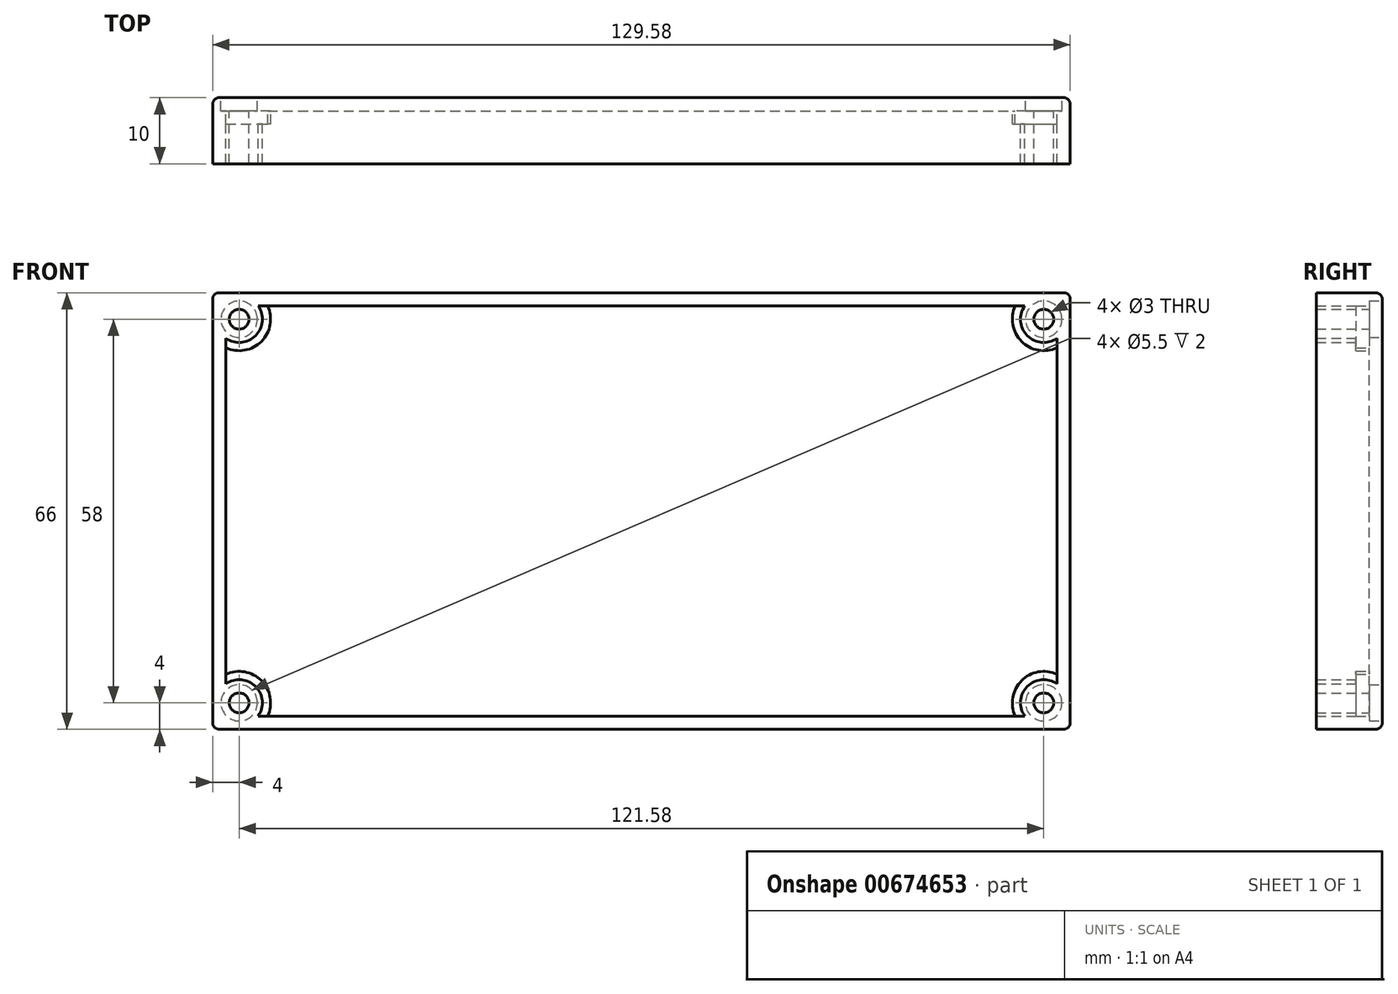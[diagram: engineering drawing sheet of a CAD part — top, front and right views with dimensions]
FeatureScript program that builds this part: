
annotation { "Feature Type Name" : "Feature", "Feature Type Description" : "" }
export const myFeature = defineFeature(function(context is Context, id is Id, definition is map)
    precondition{}
    {
        {
            var Q0;
            Q0=qCreatedBy(makeId("Front.planeOp"),FACE);
            var sketch = newSketch(context, id + "F0", { "sketchPlane" : qUnion([Q0])});
            skLineSegment(sketch, "E0.bottom", {"start": v(0, 0) * mm, "end": v(129.58, 0) * mm});
            skLineSegment(sketch, "E0.top", {"start": v(0, 66) * mm, "end": v(129.58, 66) * mm});
            skLineSegment(sketch, "E0.left", {"start": v(0, 0) * mm, "end": v(0, 66) * mm});
            skLineSegment(sketch, "E0.right", {"start": v(129.58, 0) * mm, "end": v(129.58, 66) * mm});
            skSolve(sketch);
        }
        {
            var Q0;
            Q0=makeQuery(id+"F0.imprint","IMPRINT",FACE,{"disambiguationData":[TD([[makeQuery(id+"F0.imprint","IMPRINT",EDGE,{"derivedFrom":sQuery(id+"F0.wireOp",EDGE,"E0.bottom")}),1.0]])]});
            extrude(context, id + "F1", {"entities" : qUnion([Q0]), "depth" : 10 * mm, "offsetDistance" : 25.4 * mm});
        }
        {
            var Q0;
            Q0=qCreatedBy(makeId("Front.planeOp"),FACE);
            var sketch = newSketch(context, id + "F2", { "sketchPlane" : qUnion([Q0])});
            skCircle(sketch, "E1", {"center": v(4, 62) * mm, "radius": 2.75 * mm});
            skCircle(sketch, "E2", {"center": v(125.58, 62) * mm, "radius": 2.75 * mm});
            skCircle(sketch, "E3", {"center": v(4, 4) * mm, "radius": 2.75 * mm});
            skCircle(sketch, "E4", {"center": v(125.58, 4) * mm, "radius": 2.75 * mm});
            skCircle(sketch, "E5", {"center": v(4, 62) * mm, "radius": 1.5 * mm});
            skCircle(sketch, "E6", {"center": v(4, 4) * mm, "radius": 1.5 * mm});
            skCircle(sketch, "E7", {"center": v(125.58, 4) * mm, "radius": 1.5 * mm});
            skCircle(sketch, "E8", {"center": v(125.58, 62) * mm, "radius": 1.5 * mm});
            skSolve(sketch);
        }
        {
            var Q0;
            Q0=sQuery(id+"F2.wireOp",VERTEX,"E1.center");
            var Q1;
            Q1=sQuery(id+"F2.wireOp",VERTEX,"E3.center");
            var Q2;
            Q2=sQuery(id+"F2.wireOp",VERTEX,"E4.center");
            var Q3;
            Q3=sQuery(id+"F2.wireOp",VERTEX,"E2.center");
            var Q4;
            Q4=makeQuery(id+"F1.opExtrude","SWEPT_BODY",BODY,{"disambiguationData":[OSD([sQuery(id+"F0.wireOp",EDGE,"E0.bottom"),sQuery(id+"F0.wireOp",EDGE,"E0.top"),sQuery(id+"F0.wireOp",EDGE,"E0.left"),sQuery(id+"F0.wireOp",EDGE,"E0.right")])]});
            hole(context, id + "F3", {"style" : HoleStyle.C_BORE, "endStyle" : HoleEndStyle.BLIND, "oppositeDirection" : true, "holeDiameter" : 3 * mm, "cBoreDiameter" : 5.5 * mm, "cBoreDepth" : 2 * mm, "majorDiameter" : 5 * mm, "holeDepth" : 11 * mm, "isTappedThrough" : true, "tappedDepth" : 12.7 * mm, "tapClearance" : 3, "startFromSketch" : true, "locations" : qUnion([Q0, Q1, Q2, Q3]), "scope" : qUnion([Q4])});
        }
        {
            var Q0;
            Q0=makeQuery(id+"F1.opExtrude","CAP_FACE",FACE,{"disambiguationData":[OSD([sQuery(id+"F0.wireOp",EDGE,"E0.bottom"),sQuery(id+"F0.wireOp",EDGE,"E0.top"),sQuery(id+"F0.wireOp",EDGE,"E0.left"),sQuery(id+"F0.wireOp",EDGE,"E0.right")])],"isStart":false});
            shell(context, id + "F4", {"entities" : qUnion([Q0]), "thickness" : 2 * mm});
        }
        {
            var Q0;
            Q0=makeQuery(id+"F1.opExtrude","CAP_EDGE",EDGE,{"disambiguationData":[OSD([sQuery(id+"F0.wireOp",EDGE,"E0.right")])],"isStart":true});
            var Q1;
            Q1=makeQuery(id+"F1.opExtrude","CAP_EDGE",EDGE,{"disambiguationData":[OSD([sQuery(id+"F0.wireOp",EDGE,"E0.top")])],"isStart":true});
            var Q2;
            Q2=makeQuery(id+"F1.opExtrude","CAP_EDGE",EDGE,{"disambiguationData":[OSD([sQuery(id+"F0.wireOp",EDGE,"E0.left")])],"isStart":true});
            var Q3;
            Q3=makeQuery(id+"F1.opExtrude","CAP_EDGE",EDGE,{"disambiguationData":[OSD([sQuery(id+"F0.wireOp",EDGE,"E0.bottom")])],"isStart":true});
            var Q4;
            Q4=makeQuery(id+"F1.opExtrude","SWEPT_EDGE",EDGE,{"disambiguationData":[OSD([sQuery(id+"F0.wireOp",EDGE,"E0.top"),sQuery(id+"F0.wireOp",EDGE,"E0.right")])]});
            var Q5;
            Q5=makeQuery(id+"F1.opExtrude","SWEPT_EDGE",EDGE,{"disambiguationData":[OSD([sQuery(id+"F0.wireOp",EDGE,"E0.bottom"),sQuery(id+"F0.wireOp",EDGE,"E0.right")])]});
            var Q6;
            Q6=makeQuery(id+"F1.opExtrude","SWEPT_EDGE",EDGE,{"disambiguationData":[OSD([sQuery(id+"F0.wireOp",EDGE,"E0.bottom"),sQuery(id+"F0.wireOp",EDGE,"E0.left")])]});
            var Q7;
            Q7=makeQuery(id+"F1.opExtrude","SWEPT_EDGE",EDGE,{"disambiguationData":[OSD([sQuery(id+"F0.wireOp",EDGE,"E0.top"),sQuery(id+"F0.wireOp",EDGE,"E0.left")])]});
            fillet(context, id + "F5", {"entities" : qUnion([Q0, Q1, Q2, Q3, Q4, Q5, Q6, Q7]), "radius" : 1 * mm, "tangentPropagation" : true, "allowEdgeOverflow" : false});
        }
    });
